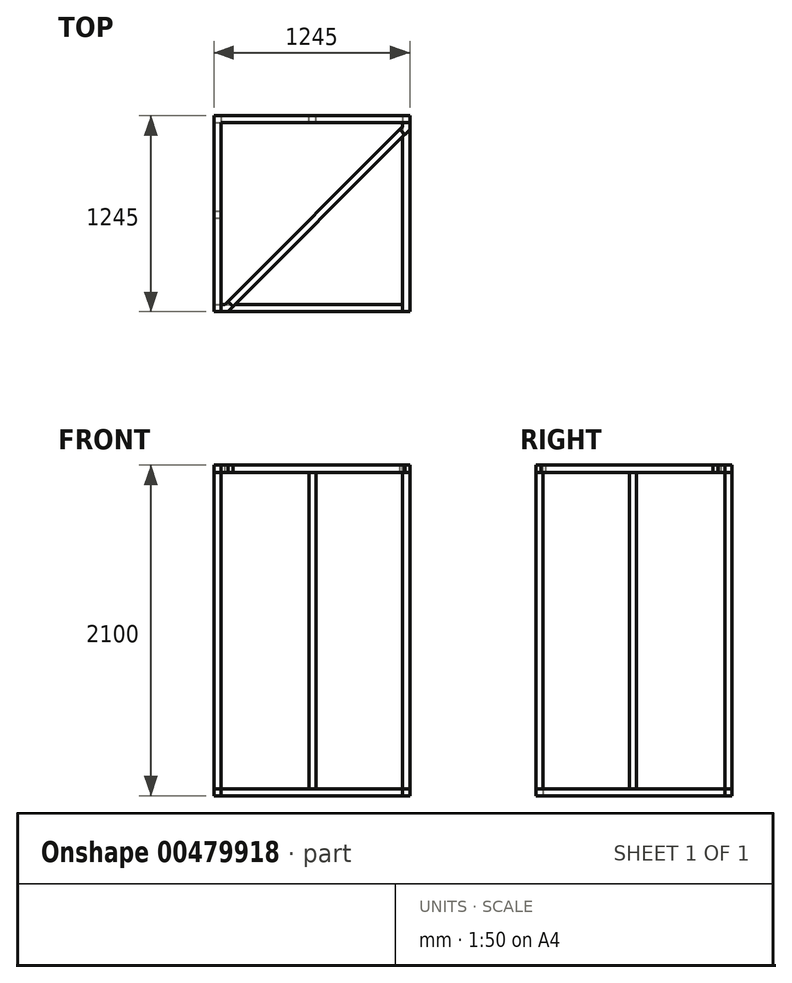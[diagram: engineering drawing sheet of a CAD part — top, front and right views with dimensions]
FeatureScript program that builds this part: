
annotation { "Feature Type Name" : "Feature", "Feature Type Description" : "" }
export const myFeature = defineFeature(function(context is Context, id is Id, definition is map)
    precondition{}
    {
        {
            var Q0;
            Q0=qCreatedBy(makeId("Top.planeOp"),FACE);
            var sketch = newSketch(context, id + "F0", { "sketchPlane" : qUnion([Q0])});
            skLineSegment(sketch, "E0.bottom", {"start": v(0, 0) * mm, "end": v(1200, 0) * mm});
            skLineSegment(sketch, "E0.left", {"start": v(0, 0) * mm, "end": v(0, -1200) * mm});
            skLineSegment(sketch, "E1.0", {"start": v(45, -45) * mm, "end": v(45, -1245) * mm});
            skLineSegment(sketch, "E1.1", {"start": v(45, -45) * mm, "end": v(1245, -45) * mm});
            skLineSegment(sketch, "E2", {"start": v(45, -1245) * mm, "end": v(0, -1245) * mm});
            skLineSegment(sketch, "E3", {"start": v(1245, -45) * mm, "end": v(1245, 0) * mm});
            skLineSegment(sketch, "E4", {"start": v(1245, 0) * mm, "end": v(1200, 0) * mm});
            skLineSegment(sketch, "E5", {"start": v(0, -1200) * mm, "end": v(0, -1245) * mm});
            skSolve(sketch);
        }
        {
            var Q0;
            Q0=makeQuery(id+"F0.imprint","IMPRINT",FACE,{"disambiguationData":[TD([[makeQuery(id+"F0.imprint","IMPRINT",EDGE,{"derivedFrom":sQuery(id+"F0.wireOp",EDGE,"E0.bottom")}),-1.0]])]});
            extrude(context, id + "F1", {"entities" : qUnion([Q0]), "depth" : 45 * mm});
        }
        {
            var Q0;
            Q0=makeQuery(id+"F1.opExtrude","CAP_FACE",FACE,{"disambiguationData":[OSD([sQuery(id+"F0.wireOp",EDGE,"E0.bottom"),sQuery(id+"F0.wireOp",EDGE,"E0.left"),sQuery(id+"F0.wireOp",EDGE,"E1.0"),sQuery(id+"F0.wireOp",EDGE,"E1.1"),sQuery(id+"F0.wireOp",EDGE,"E2"),sQuery(id+"F0.wireOp",EDGE,"E3"),sQuery(id+"F0.wireOp",EDGE,"E4"),sQuery(id+"F0.wireOp",EDGE,"E5")])],"isStart":false});
            var sketch = newSketch(context, id + "F2", { "sketchPlane" : qUnion([Q0])});
            skLineSegment(sketch, "E6.bottom", {"start": v(-1.38, 1.38) * mm, "end": v(45, 1.38) * mm});
            skLineSegment(sketch, "E6.top", {"start": v(-1.38, -45) * mm, "end": v(45, -45) * mm});
            skLineSegment(sketch, "E6.left", {"start": v(-1.38, 1.38) * mm, "end": v(-1.38, -45) * mm});
            skLineSegment(sketch, "E6.right", {"start": v(45, 1.38) * mm, "end": v(45, -45) * mm});
            skLineSegment(sketch, "E7.bottom", {"start": v(1245, 0) * mm, "end": v(1200, 0) * mm});
            skLineSegment(sketch, "E7.top", {"start": v(1245, -45) * mm, "end": v(1200, -45) * mm});
            skLineSegment(sketch, "E7.left", {"start": v(1245, 0) * mm, "end": v(1245, -45) * mm});
            skLineSegment(sketch, "E7.right", {"start": v(1200, 0) * mm, "end": v(1200, -45) * mm});
            skLineSegment(sketch, "E8.bottom", {"start": v(0, -1245) * mm, "end": v(45, -1245) * mm});
            skLineSegment(sketch, "E8.top", {"start": v(0, -1200) * mm, "end": v(45, -1200) * mm});
            skLineSegment(sketch, "E8.left", {"start": v(0, -1245) * mm, "end": v(0, -1200) * mm});
            skLineSegment(sketch, "E8.right", {"start": v(45, -1245) * mm, "end": v(45, -1200) * mm});
            skSolve(sketch);
        }
        {
            var Q0;
            {var subQ1=sQuery(id+"F2.wireOp",EDGE,"E6.top");var subQ3=makeQuery(id+"F1.opExtrude","CAP_EDGE",EDGE,{"disambiguationData":[OSD([sQuery(id+"F0.wireOp",EDGE,"E0.left"),sQuery(id+"F0.wireOp",EDGE,"E5")])],"isStart":false});var subQ4=makeQuery(id+"F2.imprint","INTERSECT",VERTEX,{"derivedFrom":[subQ3,subQ1]});Q0=makeQuery(id+"F2.imprint","IMPRINT",FACE,{"disambiguationData":[TD([[makeQuery(id+"F2.imprint","IMPRINT",EDGE,{"disambiguationData":[TD([[subQ4,-1.0]])],"derivedFrom":subQ1}),1.0]])]});}
            var Q1;
            Q1=makeQuery(id+"F2.imprint","IMPRINT",FACE,{"disambiguationData":[TD([[makeQuery(id+"F2.imprint","IMPRINT",EDGE,{"derivedFrom":sQuery(id+"F2.wireOp",EDGE,"E7.bottom")}),1.0]])]});
            var Q2;
            Q2=makeQuery(id+"F2.imprint","IMPRINT",FACE,{"disambiguationData":[TD([[makeQuery(id+"F2.imprint","IMPRINT",EDGE,{"derivedFrom":sQuery(id+"F2.wireOp",EDGE,"E8.bottom")}),-1.0]])]});
            extrude(context, id + "F3", {"entities" : qUnion([Q0, Q1, Q2]), "depth" : 2010 * mm});
        }
        {
            var Q0;
            Q0=makeQuery(id+"F3.opExtrude","CAP_FACE",FACE,{"disambiguationData":[OSD([sQuery(id+"F2.wireOp",EDGE,"E7.bottom"),sQuery(id+"F2.wireOp",EDGE,"E7.top"),sQuery(id+"F2.wireOp",EDGE,"E7.left"),sQuery(id+"F2.wireOp",EDGE,"E7.right")])],"isStart":false});
            var sketch = newSketch(context, id + "F4", { "sketchPlane" : qUnion([Q0])});
            skLineSegment(sketch, "E9.bottom", {"start": v(0, 0) * mm, "end": v(1245, 0) * mm});
            skLineSegment(sketch, "E9.top", {"start": v(0, -1245) * mm, "end": v(45, -1245) * mm});
            skLineSegment(sketch, "E9.left", {"start": v(0, 0) * mm, "end": v(0, -1245) * mm});
            skLineSegment(sketch, "E9.right", {"start": v(1245, 0) * mm, "end": v(1245, -45) * mm});
            skLineSegment(sketch, "E10", {"start": v(45, -45.33) * mm, "end": v(45, -1245) * mm});
            skLineSegment(sketch, "E11", {"start": v(45, -45.33) * mm, "end": v(1245, -45) * mm});
            skSolve(sketch);
        }
        {
            var Q0;
            Q0=makeQuery(id+"F4.imprint","IMPRINT",FACE,{"disambiguationData":[TD([[makeQuery(id+"F4.imprint","IMPRINT",EDGE,{"derivedFrom":sQuery(id+"F4.wireOp",EDGE,"E9.top")}),1.0]])]});
            var Q1;
            {var subQ0=sQuery(id+"F4.wireOp",EDGE,"E9.right");Q1=makeQuery(id+"F4.imprint","IMPRINT",FACE,{"disambiguationData":[TD([[makeQuery(id+"F4.imprint","IMPRINT",EDGE,{"derivedFrom":subQ0}),1.0]])]});}
            extrude(context, id + "F5", {"entities" : qUnion([Q0, Q1]), "depth" : 45 * mm});
        }
        {
            var Q0;
            {var subQ0=sQuery(id+"F0.wireOp",EDGE,"E1.0");var subQ1=sQuery(id+"F0.wireOp",EDGE,"E5");var subQ2=sQuery(id+"F0.wireOp",EDGE,"E1.1");var subQ3=sQuery(id+"F0.wireOp",EDGE,"E0.left");var subQ4=makeQuery(id+"F1.opExtrude","CAP_FACE",FACE,{"disambiguationData":[OSD([sQuery(id+"F0.wireOp",EDGE,"E0.bottom"),subQ3,subQ0,subQ2,sQuery(id+"F0.wireOp",EDGE,"E2"),sQuery(id+"F0.wireOp",EDGE,"E3"),sQuery(id+"F0.wireOp",EDGE,"E4"),subQ1])],"isStart":false});Q0=makeQuery(id+"F3.boolean.opBoolean","SPLIT",FACE,{"disambiguationData":[TD([makeQuery(id+"F3.opExtrude","SWEPT_FACE",FACE,{"disambiguationData":[OSD([sQuery(id+"F2.wireOp",EDGE,"E8.top")])]})])],"derivedFrom":subQ4});}
            var sketch = newSketch(context, id + "F6", { "sketchPlane" : qUnion([Q0])});
            skLineSegment(sketch, "E12.bottom", {"start": v(0, -650) * mm, "end": v(45, -650) * mm});
            skLineSegment(sketch, "E12.top", {"start": v(0, -605) * mm, "end": v(45, -605) * mm});
            skLineSegment(sketch, "E12.left", {"start": v(0, -650) * mm, "end": v(0, -605) * mm});
            skLineSegment(sketch, "E12.right", {"start": v(45, -650) * mm, "end": v(45, -605) * mm});
            skLineSegment(sketch, "E13.bottom", {"start": v(605, -45) * mm, "end": v(650, -45) * mm});
            skLineSegment(sketch, "E13.top", {"start": v(605, 0) * mm, "end": v(650, 0) * mm});
            skLineSegment(sketch, "E13.left", {"start": v(605, -45) * mm, "end": v(605, 0) * mm});
            skLineSegment(sketch, "E13.right", {"start": v(650, -45) * mm, "end": v(650, 0) * mm});
            skSolve(sketch);
        }
        {
            var Q0;
            Q0=makeQuery(id+"F6.imprint","IMPRINT",FACE,{"disambiguationData":[TD([[makeQuery(id+"F6.imprint","IMPRINT",EDGE,{"derivedFrom":sQuery(id+"F6.wireOp",EDGE,"E12.bottom")}),1.0]])]});
            var Q1;
            Q1=makeQuery(id+"F6.imprint","IMPRINT",FACE,{"disambiguationData":[TD([[makeQuery(id+"F6.imprint","IMPRINT",EDGE,{"derivedFrom":sQuery(id+"F6.wireOp",EDGE,"E13.bottom")}),1.0]])]});
            extrude(context, id + "F7", {"entities" : qUnion([Q0, Q1]), "depth" : 2010 * mm});
        }
        {
            var Q0;
            Q0=qCreatedBy(makeId("Top.planeOp"),FACE);
            var sketch = newSketch(context, id + "F8", { "sketchPlane" : qUnion([Q0])});
            skLineSegment(sketch, "E14.bottom", {"start": v(1245, -45) * mm, "end": v(1200, -45) * mm});
            skLineSegment(sketch, "E14.top", {"start": v(1245, -1245) * mm, "end": v(1200, -1245) * mm});
            skLineSegment(sketch, "E14.left", {"start": v(1245, -45) * mm, "end": v(1245, -1245) * mm});
            skLineSegment(sketch, "E14.right", {"start": v(1200, -45) * mm, "end": v(1200, -1245) * mm});
            skLineSegment(sketch, "E15.bottom", {"start": v(45, -1245) * mm, "end": v(1200, -1245) * mm});
            skLineSegment(sketch, "E15.top", {"start": v(45, -1200) * mm, "end": v(1200, -1200) * mm});
            skLineSegment(sketch, "E15.left", {"start": v(45, -1245) * mm, "end": v(45, -1200) * mm});
            skLineSegment(sketch, "E15.right", {"start": v(1200, -1245) * mm, "end": v(1200, -1200) * mm});
            skSolve(sketch);
        }
        {
            var Q0;
            Q0=makeQuery(id+"F8.imprint","IMPRINT",FACE,{"disambiguationData":[TD([[makeQuery(id+"F8.imprint","IMPRINT",EDGE,{"derivedFrom":sQuery(id+"F8.wireOp",EDGE,"E14.bottom")}),1.0]])]});
            extrude(context, id + "F9", {"entities" : qUnion([Q0]), "depth" : 45 * mm});
        }
        {
            var Q0;
            Q0=makeQuery(id+"F8.imprint","IMPRINT",FACE,{"disambiguationData":[TD([[makeQuery(id+"F8.imprint","IMPRINT",EDGE,{"derivedFrom":sQuery(id+"F8.wireOp",EDGE,"E15.bottom")}),1.0]])]});
            extrude(context, id + "F10", {"entities" : qUnion([Q0]), "depth" : 45 * mm});
        }
        {
            var Q0;
            Q0=makeQuery(id+"F5.opExtrude","CAP_FACE",FACE,{"disambiguationData":[OSD([sQuery(id+"F4.wireOp",EDGE,"E9.bottom"),sQuery(id+"F4.wireOp",EDGE,"E9.top"),sQuery(id+"F4.wireOp",EDGE,"E9.left"),sQuery(id+"F4.wireOp",EDGE,"E9.right"),sQuery(id+"F4.wireOp",EDGE,"E10"),sQuery(id+"F4.wireOp",EDGE,"E11")])],"isStart":false});
            var sketch = newSketch(context, id + "F11", { "sketchPlane" : qUnion([Q0])});
            skLineSegment(sketch, "E16", {"start": v(1245, -45) * mm, "end": v(1200, -45.01) * mm});
            skLineSegment(sketch, "E17", {"start": v(1200, -45.01) * mm, "end": v(1200, -71.13) * mm});
            skLineSegment(sketch, "E18", {"start": v(1200, -71.13) * mm, "end": v(1181.65, -89.48) * mm});
            skLineSegment(sketch, "E19", {"start": v(1181.65, -89.48) * mm, "end": v(1213.38, -121.2) * mm});
            skLineSegment(sketch, "E20", {"start": v(1213.38, -121.2) * mm, "end": v(1245, -89.59) * mm});
            skLineSegment(sketch, "E21", {"start": v(1245, -89.59) * mm, "end": v(1245, -45) * mm});
            skLineSegment(sketch, "E22", {"start": v(1197.52, -105.35) * mm, "end": v(1257.83, -45.03) * mm, "construction": true});
            skLineSegment(sketch, "E23", {"start": v(1197.52, -105.35) * mm, "end": v(1137.2, -45.03) * mm, "construction": true});
            skLineSegment(sketch, "E24", {"start": v(1137.2, -45.03) * mm, "end": v(1257.83, -45.03) * mm, "construction": true});
            skSolve(sketch);
        }
        {
            var Q0;
            {var subQ0=sQuery(id+"F11.wireOp",EDGE,"E16");Q0=makeQuery(id+"F11.imprint","IMPRINT",FACE,{"disambiguationData":[TD([[makeQuery(id+"F11.imprint","IMPRINT",EDGE,{"derivedFrom":subQ0}),1.0]])]});}
            var sketch = newSketch(context, id + "F12", { "sketchPlane" : qUnion([Q0])});
            skLineSegment(sketch, "E25", {"start": v(45, -1245) * mm, "end": v(45, -1200) * mm});
            skLineSegment(sketch, "E26", {"start": v(45, -1200) * mm, "end": v(70.9, -1200) * mm});
            skLineSegment(sketch, "E27", {"start": v(70.9, -1200) * mm, "end": v(89.36, -1181.5) * mm});
            skLineSegment(sketch, "E28", {"start": v(89.36, -1181.5) * mm, "end": v(121.2, -1213.31) * mm});
            skLineSegment(sketch, "E29", {"start": v(121.2, -1213.31) * mm, "end": v(89.55, -1245) * mm});
            skLineSegment(sketch, "E30", {"start": v(89.55, -1245) * mm, "end": v(45, -1245) * mm});
            skLineSegment(sketch, "E31", {"start": v(105.28, -1197.4) * mm, "end": v(45, -1257.76) * mm, "construction": true});
            skLineSegment(sketch, "E32", {"start": v(45, -1137.2) * mm, "end": v(45, -1257.76) * mm, "construction": true});
            skLineSegment(sketch, "E33", {"start": v(105.28, -1197.4) * mm, "end": v(45, -1137.2) * mm, "construction": true});
            skSolve(sketch);
        }
        {
            var Q0;
            Q0=makeQuery(id+"F12.imprint","IMPRINT",FACE,{"disambiguationData":[TD([[makeQuery(id+"F12.imprint","IMPRINT",EDGE,{"derivedFrom":sQuery(id+"F12.wireOp",EDGE,"E25")}),-1.0]])]});
            var Q1;
            Q1=makeQuery(id+"F11.imprint","IMPRINT",FACE,{"disambiguationData":[TD([[makeQuery(id+"F11.imprint","IMPRINT",EDGE,{"derivedFrom":sQuery(id+"F11.wireOp",EDGE,"E16")}),-1.0]])]});
            extrude(context, id + "F13", {"entities" : qUnion([Q0, Q1]), "oppositeDirection" : true, "depth" : 45 * mm});
        }
        {
            var Q0;
            Q0=makeQuery(id+"F13.opExtrude","SWEPT_FACE",FACE,{"disambiguationData":[OSD([sQuery(id+"F12.wireOp",EDGE,"E28")])]});
            extrude(context, id + "F14", {"entities" : qUnion([Q0]), "endBound" : BoundingType.UP_TO_NEXT, "depth" : 25 * mm});
        }
    });
